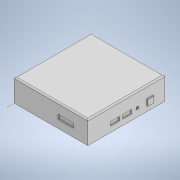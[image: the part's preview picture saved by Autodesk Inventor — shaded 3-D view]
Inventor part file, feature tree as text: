
AUTODESK INVENTOR PART (.ipt)
format: ipt  version: 2020 (Build 240168000, 168)  size: 256,512 bytes
history: native  units: mm
features: sketch x12, extrude x9, hole x3, fillet x1, other x1, pattern_linear x1
ambient origin geometry x8: Origin, YZ Plane, XZ Plane, XY Plane, X Axis, Y Axis, Z Axis, Center Point
bodies: Solid1 (feature_tree)
feature tree (27):
  extrude  "Extrusion1"  Depth=117.0mm
  fillet  "Fillet1"  Radius=34.19mm
  extrude  "Extrusion2"  Depth=2.0mm
  hole  "Hole2"  [1 undecoded]
  other  "Work Axis1"
  pattern_linear  "Rectangular Pattern1"  Count1=2 Spacing1=91.0mm
  extrude  "Extrusion3"  Depth=1.0mm
  hole  "Hole3"  [1 undecoded]
  hole  "Hole4"  [1 undecoded]
  extrude  "Extrusion4"  Depth=8.6mm
  extrude  "Extrusion5"  Depth=4.86mm
  extrude  "Extrusion6"  Depth=1.5mm TaperAngle=0.0deg
  extrude  "Extrusion7"  Depth=2.0mm
  extrude  "Extrusion8"  Depth=1.5mm
  extrude  "Extrusion9"  Depth=1.5mm
  sketch  "Sketch1"  dims[d0=111.85mm d1=117.0mm d2=34.19mm d3=0.0mm]
  sketch  "Sketch2"  dims[d4=2.0mm d5=10.75mm]
  sketch  "Sketch4"  dims[d6=10.5mm d7=10.5mm d8=20.0mm d10=91.0mm d11=20.0mm d13=95.0mm]
  sketch  "Sketch5"  dims[d16=1.5mm d17=0.0mm]
  sketch  "Sketch6"  dims[d25=3.0mm d26=6.0mm d27=4.0mm d28=2.0mm d29=90.0deg d30=1.0mm d31=20.594885mm d32=13.3mm]
  sketch  "Sketch7"  dims[d33=58.5mm d34=20.0mm d36=84.5mm]
  sketch  "Sketch8"  dims[d37=13.6mm d38=5.9mm]
  sketch  "Sketch10"  dims[d39=13.6mm d40=5.9mm d41=8.6mm]
  sketch  "Sketch11"  dims[d42=34.3mm d43=4.86mm]
  sketch  "Sketch12"  dims[d44=8.6mm d45=1.5mm d46=0.0mm]
  sketch  "Sketch13"  dims[d47=4.24mm d48=5.98424mm d49=4.0mm d50=2.0mm d51=90.0deg d52=10.688mm d53=20.594885mm d54=8.9mm]
  sketch  "Sketch14"  dims[d55=12.0mm d56=9.25mm d57=6.88mm d58=5.98424mm d59=4.0mm d60=2.0mm d61=90.0deg d62=10.688mm d63=20.594885mm d64=20.0mm d65=16.12mm d66=6.56mm d67=10.5mm d68=8.31mm d69=1.55mm d70=1.55mm d71=8.814281mm d72=1.5mm d73=0.0mm d81=15.55mm d82=11.7mm d84=5.0mm d85=7.1mm d86=1.5mm d87=0.0mm d88=14.3mm d89=6.6mm d90=12.14mm d91=4.4mm d92=14.3mm d93=6.6mm d94=2.4mm d95=4.4mm d96=1.5mm d97=0.0mm d98=10.15mm d99=10.82mm d100=7.28mm d101=1.5mm d102=0.0mm d103=14.3mm d104=7.6mm d105=9.2mm d106=9.2mm d107=1.5mm d108=0.0mm d109=23.5mm d110=6.57mm d111=12.25mm d112=21.7mm d113=1.5mm d114=0.0mm]
note: 3 required parameter values undecoded (feature->parameter linkage not recoverable at this tier; creation-order binding heuristic only, values carry confidence <= 0.55)
